# Revit family: Haworth_ComposeStorage_Tower_Wardrobe
name_source: partatom
category: Furniture Systems
revit_build: Autodesk Revit 2018 (Build: 20170223_1515(x64)
units: mm (PartAtom-declared; Revit-internal decimal feet)

## family parameters
Always vertical = Yes
Cut with Voids When Loaded = No
OmniClass Number = 23.40.70.14.64.21
OmniClass Title = Systems Furniture
Part Type = Normal
Room Calculation Point = No
Round Connector Dimension = Use Diameter
Shared = No
Work Plane-Based = No

## types (12) — shared parameters
Actual Width = 23 7/8"
Assembly Code = E2020200
Base = Yes
Base Finish = Haworth _ Wood _ White Oak
Base Height = 1"
Box Box File = Yes
Cabinet Finish = Haworth _ Wood _ White Oak
Chamfer Legs = No
Classic Pull = No
Crescent Pull = No
Custom Size = No
Description = Haworth - Compose Storage Tower - File Wardrobe
Door Finish = Haworth _ Wood _ White Oak
Door Width = 8 7/16"
Drawer Height Bottom = 13"
Drawer Height Middle = 5 15/16"
Drawer Height Top = 5 15/16"
Drawer Width = 15 5/16"
File File = No
Finished Back = No
J Pull = No
Linear Pull = No
Manufacturer = Haworth
Max. Depth = 29 5/8"
Max. Height = 73"
Max. Width = 23 7/8"
Min. Depth = 17 5/8"
Min. Height = 49"
Min. Width = 23 7/8"
Min/Max Depth = 18, 24, 30 in.
Min/Max Height = 49, 57, 65, 73 in.
Model = BZVH
Patterns Pull = Yes
Plynth Base = No
Pull Finish = Haworth _ Metal _ Brushed Aluminum
Revision Number = 3
Side Panel Base = Yes
Size = Verify Final Dim. w/ Haworth
Sustainability Info = http://media.haworth.com
URL = www.haworth.com
URL - Product = http://www.haworth.com
Warranty = http://www.haworth.com
Width = 24"

## per-type parameters (varying)
| type | Actual Depth | Actual Height | Base Depth | Depth | Height |
| 18d 49h | 17 5/8" | 49" | 16 7/8" | 18" | 49" |
| 18d 57h | 17 5/8" | 57" | 16 7/8" | 18" | 57" |
| 18d 65h | 17 5/8" | 65" | 16 7/8" | 18" | 65" |
| 18d 73h | 17 5/8" | 73" | 16 7/8" | 18" | 73" |
| 24d 49h | 23 5/8" | 49" | 22 7/8" | 24" | 49" |
| 24d 57h | 23 5/8" | 57" | 22 7/8" | 24" | 57" |
| 24d 65h | 23 5/8" | 65" | 22 7/8" | 24" | 65" |
| 24d 73h | 23 5/8" | 73" | 22 7/8" | 24" | 73" |
| 30d 49h | 29 1/4" | 49" | 28 1/2" | 30" | 49" |
| 30d 57h | 29 1/4" | 57" | 28 1/2" | 30" | 57" |
| 30d 65h | 29 1/4" | 65" | 28 1/2" | 30" | 65" |
| 30d 73h | 29 1/4" | 73" | 28 1/2" | 30" | 73" |

## geometry (parser evidence)
native form markers: Sweep x11
no freeform markers — native parametric forms only
